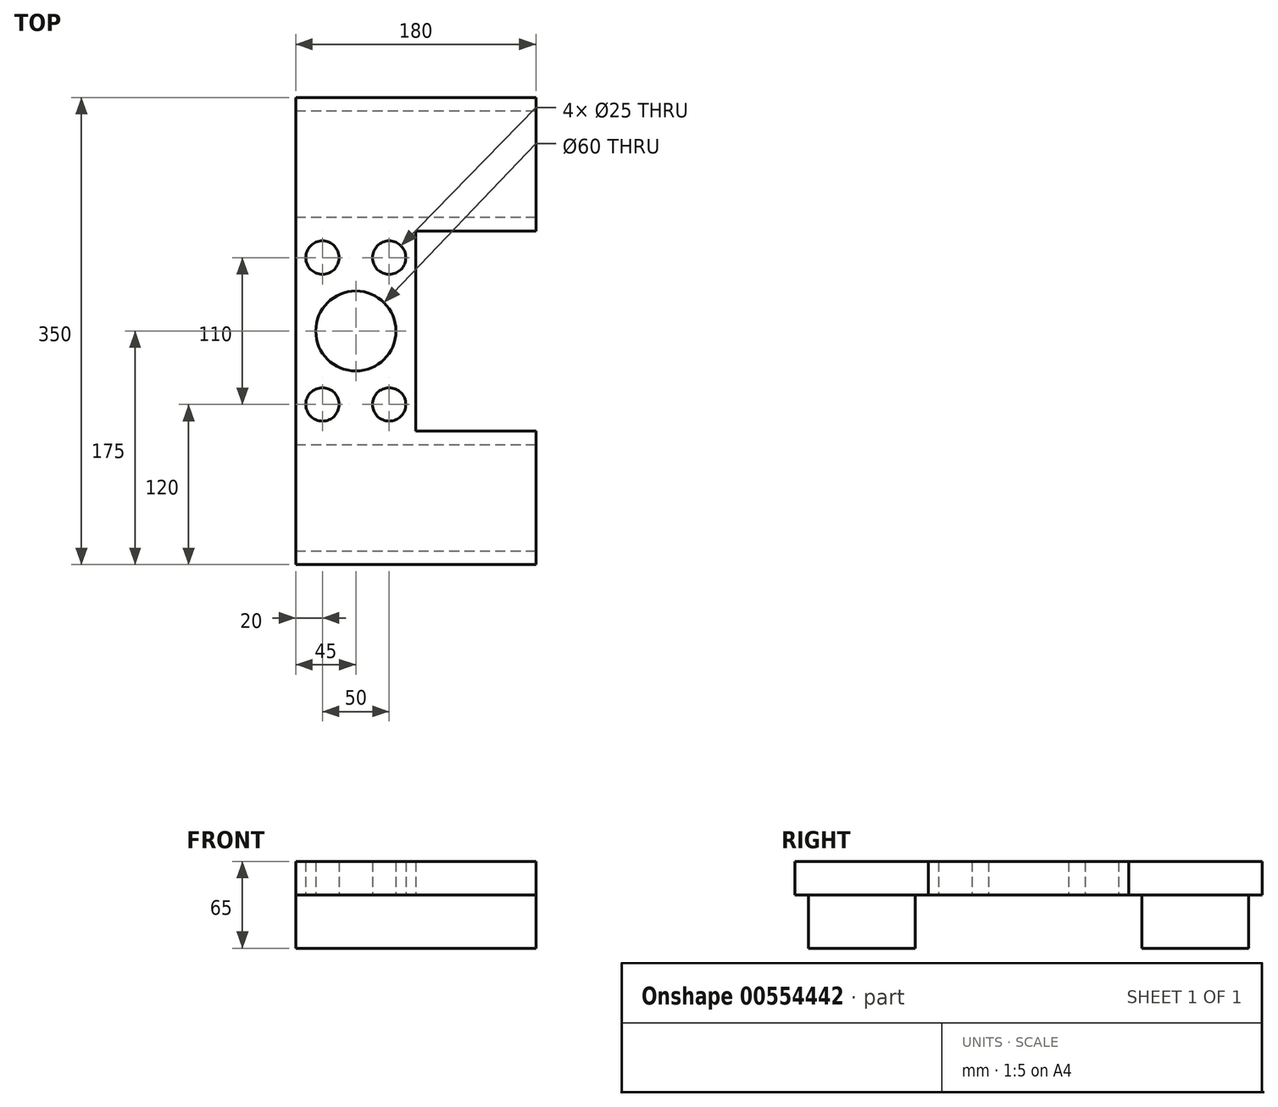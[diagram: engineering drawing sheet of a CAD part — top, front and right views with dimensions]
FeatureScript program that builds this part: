
annotation { "Feature Type Name" : "Feature", "Feature Type Description" : "" }
export const myFeature = defineFeature(function(context is Context, id is Id, definition is map)
    precondition{}
    {
        {
            var Q0;
            Q0=qCreatedBy(makeId("Top.planeOp"),FACE);
            var sketch = newSketch(context, id + "F0", { "sketchPlane" : qUnion([Q0])});
            skLineSegment(sketch, "E0", {"start": v(65, 175) * mm, "end": v(-115, 175) * mm});
            skLineSegment(sketch, "E1", {"start": v(-115, 175) * mm, "end": v(-115, -175) * mm});
            skLineSegment(sketch, "E2", {"start": v(-115, -175) * mm, "end": v(65, -175) * mm});
            skLineSegment(sketch, "E3", {"start": v(65, -175) * mm, "end": v(65, -75) * mm});
            skLineSegment(sketch, "E4", {"start": v(65, -75) * mm, "end": v(-25, -75) * mm});
            skLineSegment(sketch, "E5", {"start": v(-25, 75) * mm, "end": v(65, 75) * mm});
            skLineSegment(sketch, "E6", {"start": v(65, 75) * mm, "end": v(65, 175) * mm});
            skLineSegment(sketch, "E7", {"start": v(-25, 75) * mm, "end": v(-25, 0) * mm});
            skLineSegment(sketch, "E8", {"start": v(-25, 0) * mm, "end": v(-25, -75) * mm});
            skCircle(sketch, "E9", {"center": v(-95, 55) * mm, "radius": 12.5 * mm});
            skCircle(sketch, "E10", {"center": v(-45, 55) * mm, "radius": 12.5 * mm});
            skCircle(sketch, "E11", {"center": v(-95, -55) * mm, "radius": 12.5 * mm});
            skCircle(sketch, "E12", {"center": v(-45, -55) * mm, "radius": 12.5 * mm});
            skLineSegment(sketch, "E13", {"start": v(85.88, 75) * mm, "end": v(-143.58, 75) * mm, "construction": true});
            skLineSegment(sketch, "E14", {"start": v(85.88, -75) * mm, "end": v(-143.58, -75) * mm, "construction": true});
            skPoint(sketch, "E14.endSnap0", {"position": v(20, -75) * mm});
            skCircle(sketch, "E15", {"center": v(-70, 0) * mm, "radius": 30 * mm});
            skPoint(sketch, "E15.centerSnap0", {"position": v(-115, 0) * mm});
            skSolve(sketch);
        }
        {
            var Q0;
            Q0=makeQuery(id+"F0.imprint","IMPRINT",FACE,{"disambiguationData":[TD([[makeQuery(id+"F0.imprint","IMPRINT",EDGE,{"derivedFrom":sQuery(id+"F0.wireOp",EDGE,"E0")}),1.0]])]});
            extrude(context, id + "F1", {"entities" : qUnion([Q0]), "depth" : 25 * mm, "offsetDistance" : 25 * mm});
        }
        {
            var Q0;
            Q0=qCreatedBy(makeId("Top.planeOp"),FACE);
            var sketch = newSketch(context, id + "F2", { "sketchPlane" : qUnion([Q0])});
            skLineSegment(sketch, "E16", {"start": v(0, 0) * mm, "end": v(-175.24, 0) * mm, "construction": true});
            skLineSegment(sketch, "E17", {"start": v(-115, 188.46) * mm, "end": v(-115, -195.72) * mm, "construction": true});
            skLineSegment(sketch, "E18", {"start": v(65, -195.72) * mm, "end": v(65, 188.46) * mm, "construction": true});
            skLineSegment(sketch, "E19", {"start": v(65, -165) * mm, "end": v(-115, -165) * mm});
            skLineSegment(sketch, "E20", {"start": v(-115, -165) * mm, "end": v(-115, -85) * mm});
            skLineSegment(sketch, "E21", {"start": v(-115, -85) * mm, "end": v(65, -85) * mm});
            skLineSegment(sketch, "E22", {"start": v(65, -85) * mm, "end": v(65, -165) * mm});
            skLineSegment(sketch, "E23", {"start": v(65, 85) * mm, "end": v(-115, 85) * mm});
            skLineSegment(sketch, "E24", {"start": v(-115, 85) * mm, "end": v(-115, 165) * mm});
            skLineSegment(sketch, "E25", {"start": v(-115, 165) * mm, "end": v(65, 165) * mm});
            skLineSegment(sketch, "E26", {"start": v(65, 165) * mm, "end": v(65, 85) * mm});
            skSolve(sketch);
        }
        {
            var Q0;
            Q0 = qSketchRegion(id + "F2", true);
            extrude(context, id + "F3", {"entities" : qUnion([Q0]), "oppositeDirection" : true, "depth" : 40 * mm, "offsetDistance" : 25 * mm});
        }
    });
